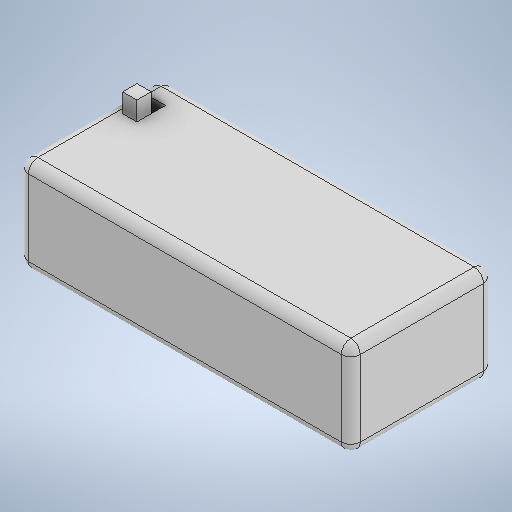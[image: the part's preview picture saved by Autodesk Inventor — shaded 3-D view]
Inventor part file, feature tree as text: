
AUTODESK INVENTOR PART (.ipt)
format: ipt  version: 2025.2 (Build 292293000, 293)  size: 239,616 bytes
history: native  units: mm
features: extrude x3, sketch x3, fillet x2
ambient origin geometry x8: Origin, YZ Plane, XZ Plane, XY Plane, X Axis, Y Axis, Z Axis, Center Point
bodies: Solid1 (feature_tree)
feature tree (8):
  extrude  "Extrusion1"  Depth=30.0mm
  fillet  "Fillet1"  Radius=20.0mm
  sketch  "Sketch2"  dims[d5=2.0mm d6=3.0mm]
  fillet  "Fillet2"  Radius=2.0mm
  extrude  "Extrusion2"  Depth=3.0mm
  extrude  "Extrusion3"  Depth=4.0mm TaperAngle=0.0deg
  sketch  "Sketch1"  dims[d0=70.0mm d1=30.0mm d2=20.0mm d3=0.0mm d4=2.0mm]
  sketch  "Sketch3"  dims[d7=6.0mm d8=4.0mm d9=0.0mm d10=8.0mm d11=0.0mm]
